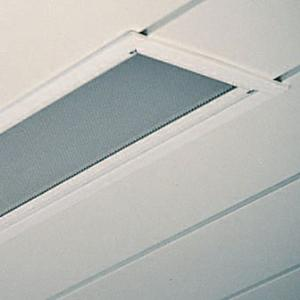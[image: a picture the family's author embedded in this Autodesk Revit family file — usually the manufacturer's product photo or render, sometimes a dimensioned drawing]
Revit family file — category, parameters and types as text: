
# Revit family: 3f_filippi_-_l_560_sp_3f_filippi_-_270961_-_l_561x30w_led_sp_221x1556
name_source: partatom
category: Lighting Fixtures
units: mm (PartAtom-declared; Revit-internal decimal feet)

## family parameters
Cut with Voids When Loaded = No
Host = Face
Light Source = No
Part Type = Normal
Room Calculation Point = No
Round Connector Dimension = Use Diameter
Shared = No

## types (1)
- 3F Filippi - L 560 SP (1 x LED, 3674 lm, 34 W, 4000 K)
    Apparent Load = 34 VA
    Approval mark = ENEC
    CIE Flux Codes = 64 90 98 100 100
    Color Rendering = 80
    Color Temperature = 4000 K
    Control Gear = Electronic ballast
    Default Elevation = 1800 mm
    Description = ILLUMINOTECHNICAL
Luminous efficiency 100% (DLOR 100%, ULOR 0%).
Initial luminous flux of the luminaire 3674 lm.
Direct symmetric distribution.
Installation Interdistance Transv.D = 1.08 x hu - Long.D = 1.18 x hu.
Tabular UGR (CIE 117 - 4H-8H; S=0.25H; 70/50/20): RUG 17.3 - 19.7.
Beam angle: 70° - 94°.
Luminous efficacy 108 lm/W.
Lifetime (L93/B10): 30000 h. (tq+25°C)
Lifetime (L90/B10): 50000 h. (tq+25°C)
Lifetime (L85/B10): 80000 h. (tq+25°C)
Lifetime (L80/B10): 100000 h. (tq+25°C)
Sudden decreased luminous flux after 50000 hours: 0% (C0).
Photobiological safety in compliance with IEC/TR 62778: RG0 risk exempt, (IEC 62471).
In compliance with IEC/EN 62722-2-1 - IEC/EN 62717 standards.

SOURCE
Linear LED module 30W/840.
Energy efficiency class (UE 2019/2020 - UE 2019/2015): D.
CIE 13.3 Colour rendering index: CRI >80 (R9 <50%).
IES TM-30 Fidelity Index: Rf = 84 Rg = 95.
CCT nominal colour temperature 4000 K.
Colour initial tolerance (MacAdam): SDCM 3.

MECHANICAL
Housing in galvannealed steel, painted in white epoxy-polyester.
SP transparent methacrylate (PMMA) flat diffuser, externally multilenticular, anti-glare, injection moulded, locked to the white painted aluminium perimetrical frame, hinged opening.
Luminaire with limited surface temperature. - D - (EN 60598-2-24)
Dimensions: 1556x221 mm, height 95 mm. Weight 6.43 kg.
IP54 protection degree for exposed part, IP20 for recessed part.
Mechanical strength to impacts IK06 (1 joule).
Glow-wire test resistance 650°C.

ELECTRICAL
Halogen Free electronic wiring 230V-50/60Hz, power factor 0.90, THD <25%, constant output current, SELV, class I, 1 driver.
Power of the luminaire 34 W.
CE - IEC 60598-1 - EN 60598-1.
SAFE FLICKER: PstLM=<1 and SVM=<0.4 (IEC TR 61547-1 and IEC TR 63158), to ensure a more comfortable and safe light.
Luminaire compliant with EN 60598-2-22 for power supply from a centralised emergency system CPSS (Central Power Supply System), not incorporated in the luminaire - high risk areas excluded. The default power and flux are 100% in AC and 100% in DC.
Ambient temperature from 0°C to +25°C.
Temperature class T6 max 85°C.
Relative humidity UR: <85%.

INSTALLATION
Pull-up recessed fitting / Slat ceiling recessed fitting.
False ceiling carving: 190x1530 mm.
All accessories dedicated to this product are available on the Catalog and on our website www.3F-Filippi.com.

APPLICATIONS
Suitable product for food production plants (HACCP), IFS (Food Version 6), BRC (GSFS Food Version 7).
Recessed installation in environments requiring protection, good visual comfort with lamp shielding and simplified cleaning.

WARNING
Luminaire designed for disposal/recycling at end-of-life.
Replaceable (LED only) light source by a professional. Replaceable control gear by a professional.
    Height = 0 mm  [stored 0 ft]
    Lamp = 1 x LED
    Lamp Light Flux = 3674 lm
    Lamp Power = 34 W
    Lamp count = 1
    Length = 1556 mm
    Lifetime = 50000 h
    Luminous efficacy = 108 lm/W
    Manufacturer = 3F Filippi
    ModVariant = No
    Model = 3F Filippi - 270961 - L 561x30W LED SP 221x1556
    Mounting Place = Ceiling
    Mounting Type = Recessed
    Number of Poles = 1
    OnlyDefault = Yes
    Power Factor = 1
    Product Name = 3F Filippi - L 560 SP
    Product group = recessed luminaire
    ProductGroupID = 4
    Protection Class = Protection class I
    Protection Degree = IP 20
    RLX_Detail_Level = 1
    RLX_Emergency_Light_Flux = 0 lm
    RLX_Emergency_Type = 0
    RLX_Emergency_Type_DB = No
    RlxData = <blob elided: 84289 chars, md5=1e6b0e5c>
    Socket = socket
    Standby Power = 0 W
    System Light Flux = 3674 lm
    System Power = 34 W
    Type Comments = Product without accessories
    Type Image = 3ffilippi_270961.jpg
    URL = http://relux.com
    VarID = ---
    Voltage = 0 V
    Weight = 0.00 kg
    Width = 221 mm

note: [stored X ft] marks values corroborated as IEEE doubles in the binary element streams (Revit-internal decimal feet)

## geometry (parser evidence)
native form markers: Blend x4, Sweep x13
no freeform markers — native parametric forms only
